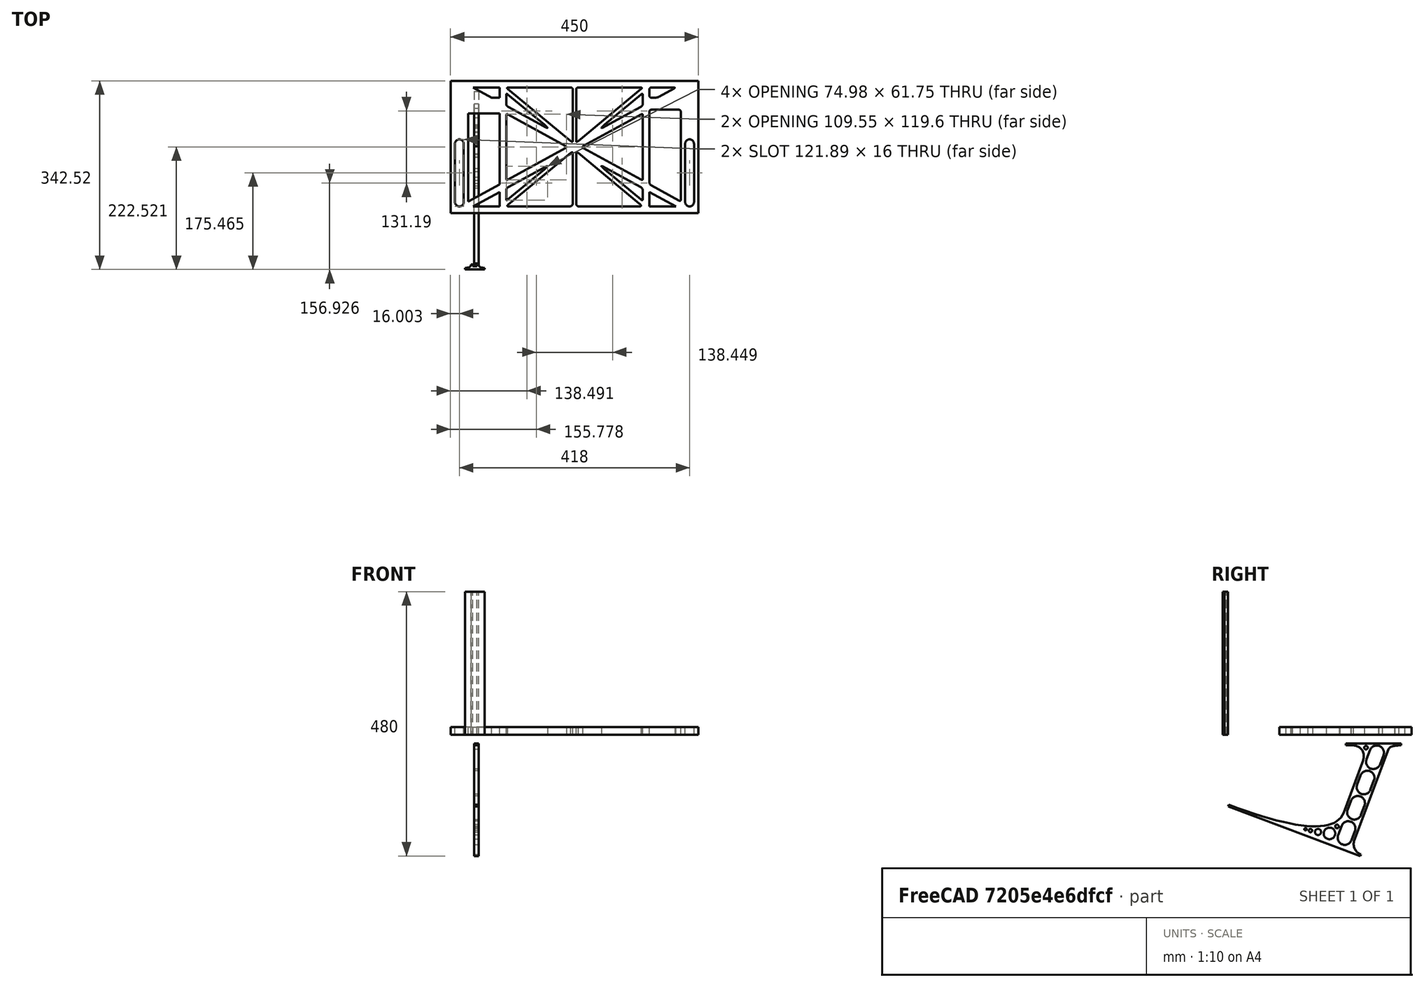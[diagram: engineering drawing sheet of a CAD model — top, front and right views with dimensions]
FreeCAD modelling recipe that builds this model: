
FCSTD DOCUMENT  (FreeCAD 0.19R0.19.2)
Label: laptopStand107
License: All rights reserved
LicenseURL: http://en.wikipedia.org/wiki/All_rights_reserved
objects: Sketcher::SketchObject×3, Part::Extrusion×3
note: 6 computed .brp shape members not serialized (recipe doc carries the construction recipe); baked Part::Feature solids carry a one-line shape summary decoded from their .brp

FEATURE [Sketcher::SketchObject] Sketch
  FullyConstrained = true
  sketch-geometry (292):
    g0: LineSegment StartX=-10.9272 StartY=-82.7794 StartZ=0 EndX=46.0728 EndY=-51.4823 EndZ=0
    g1: LineSegment StartX=366.073 StartY=-91.7794 StartZ=0 EndX=318.073 EndY=-65.424 EndZ=0
    g2: LineSegment StartX=-10.9272 StartY=77.3346 StartZ=0 EndX=-10.9272 EndY=-82.7794 EndZ=0
    g3: LineSegment StartX=-1.92719 StartY=-91.7794 StartZ=0 EndX=46.0728 EndY=-91.7794 EndZ=0
    g4: LineSegment StartX=318.073 StartY=-65.424 StartZ=0 EndX=318.073 EndY=-91.7794 EndZ=0
    g5: LineSegment StartX=318.073 StartY=-91.7794 StartZ=0 EndX=366.073 EndY=-91.7794 EndZ=0
    g6: LineSegment StartX=46.0728 StartY=-65.424 StartZ=0 EndX=-1.92719 EndY=-91.7794 EndZ=0
    g7: LineSegment StartX=46.0728 StartY=-65.424 StartZ=0 EndX=46.0728 EndY=-91.7794 EndZ=0
    g8: LineSegment StartX=46.0728 StartY=77.3346 StartZ=0 EndX=46.0728 EndY=-51.4823 EndZ=0
    g9: LineSegment StartX=-42.9272 StartY=136.221 StartZ=0 EndX=-42.9272 EndY=-103.779 EndZ=0
    g10: LineSegment StartX=407.073 StartY=136.221 StartZ=0 EndX=407.073 EndY=-103.779 EndZ=0
    g11: ArcOfCircle CenterX=-26.9272 CenterY=22.1087 CenterZ=0 NormalX=0 NormalY=0 NormalZ=1 AngleXU=0 Radius=8 StartAngle=1e-16 EndAngle=3.14159
    g12: ArcOfCircle CenterX=-26.9272 CenterY=-83.7794 CenterZ=0 NormalX=0 NormalY=0 NormalZ=1 AngleXU=0 Radius=8 StartAngle=3.14159 EndAngle=6.28319
    g13: LineSegment StartX=-34.9272 StartY=22.1087 StartZ=0 EndX=-34.9272 EndY=-83.7794 EndZ=0
    g14: LineSegment StartX=-18.9272 StartY=22.1087 StartZ=0 EndX=-18.9272 EndY=-83.7794 EndZ=0
    g15: ArcOfCircle CenterX=391.073 CenterY=22.1087 CenterZ=0 NormalX=0 NormalY=0 NormalZ=1 AngleXU=0 Radius=8 StartAngle=-4.4e-15 EndAngle=3.14159
    g16: LineSegment StartX=399.073 StartY=22.1087 StartZ=0 EndX=399.073 EndY=-83.7794 EndZ=0
    g17: LineSegment StartX=383.073 StartY=22.1087 StartZ=0 EndX=383.073 EndY=-83.7794 EndZ=0
    g18: ArcOfCircle CenterX=391.073 CenterY=-83.7794 CenterZ=0 NormalX=0 NormalY=0 NormalZ=1 AngleXU=0 Radius=8 StartAngle=3.14159 EndAngle=6.28319
    g19: Circle CenterX=175.022 CenterY=27.0628 CenterZ=0 NormalX=0 NormalY=0 NormalZ=1 AngleXU=0 Radius=1
    g20: Circle CenterX=179.022 CenterY=24.8665 CenterZ=0 NormalX=0 NormalY=0 NormalZ=1 AngleXU=0 Radius=1
    g21: Circle CenterX=179.022 CenterY=27.0628 CenterZ=0 NormalX=0 NormalY=0 NormalZ=1 AngleXU=0 Radius=1
    g22: BSplineCurve PolesCount=3 KnotsCount=2 Degree=2 IsPeriodic=0
    g23: GeomPoint X=175.022 Y=27.0628 Z=0
    g24: GeomPoint X=179.022 Y=27.0628 Z=0
    g25: Circle CenterX=189.124 CenterY=27.0628 CenterZ=0 NormalX=0 NormalY=0 NormalZ=1 AngleXU=0 Radius=1
    g26: Circle CenterX=185.124 CenterY=24.8665 CenterZ=0 NormalX=0 NormalY=0 NormalZ=1 AngleXU=0 Radius=1
    g27: Circle CenterX=185.124 CenterY=27.0628 CenterZ=0 NormalX=0 NormalY=0 NormalZ=1 AngleXU=0 Radius=1
    g28: BSplineCurve PolesCount=3 KnotsCount=2 Degree=2 IsPeriodic=0
    g29: GeomPoint X=189.124 Y=27.0628 Z=0
    g30: GeomPoint X=185.124 Y=27.0628 Z=0
    g31: Circle CenterX=175.022 CenterY=5.37834 CenterZ=0 NormalX=0 NormalY=0 NormalZ=1 AngleXU=0 Radius=1
    g32: Circle CenterX=179.022 CenterY=7.57463 CenterZ=0 NormalX=0 NormalY=0 NormalZ=1 AngleXU=0 Radius=1
    g33: Circle CenterX=179.022 CenterY=5.34704 CenterZ=0 NormalX=0 NormalY=0 NormalZ=1 AngleXU=0 Radius=1
    g34: BSplineCurve PolesCount=3 KnotsCount=2 Degree=2 IsPeriodic=0
    g35: GeomPoint X=175.022 Y=5.37834 Z=0
    g36: GeomPoint X=179.022 Y=5.34704 Z=0
    g37: Circle CenterX=189.124 CenterY=5.37834 CenterZ=0 NormalX=0 NormalY=0 NormalZ=1 AngleXU=0 Radius=1
    g38: Circle CenterX=185.124 CenterY=7.57463 CenterZ=0 NormalX=0 NormalY=0 NormalZ=1 AngleXU=0 Radius=1
    g39: Circle CenterX=185.124 CenterY=5.34704 CenterZ=0 NormalX=0 NormalY=0 NormalZ=1 AngleXU=0 Radius=1
    g40: BSplineCurve PolesCount=3 KnotsCount=2 Degree=2 IsPeriodic=0
    g41: GeomPoint X=189.124 Y=5.37834 Z=0
    g42: GeomPoint X=185.124 Y=5.34704 Z=0
    g43: Circle CenterX=165.871 CenterY=18.1458 CenterZ=0 NormalX=0 NormalY=0 NormalZ=1 AngleXU=0 Radius=1
    g44: Circle CenterX=169.377 CenterY=16.2206 CenterZ=0 NormalX=0 NormalY=0 NormalZ=1 AngleXU=0 Radius=1
    g45: Circle CenterX=165.871 CenterY=14.2954 CenterZ=0 NormalX=0 NormalY=0 NormalZ=1 AngleXU=0 Radius=1
    g46: BSplineCurve PolesCount=3 KnotsCount=2 Degree=2 IsPeriodic=0
    g47: GeomPoint X=165.871 Y=18.1458 Z=0
    g48: GeomPoint X=165.871 Y=14.2954 Z=0
    g49: Circle CenterX=198.275 CenterY=18.1458 CenterZ=0 NormalX=0 NormalY=0 NormalZ=1 AngleXU=0 Radius=1
    g50: Circle CenterX=194.768 CenterY=16.2206 CenterZ=0 NormalX=0 NormalY=0 NormalZ=1 AngleXU=0 Radius=1
    g51: Circle CenterX=198.275 CenterY=14.2954 CenterZ=0 NormalX=0 NormalY=0 NormalZ=1 AngleXU=0 Radius=1
    g52: BSplineCurve PolesCount=3 KnotsCount=2 Degree=2 IsPeriodic=0
    g53: GeomPoint X=198.275 Y=18.1458 Z=0
    g54: GeomPoint X=198.275 Y=14.2954 Z=0
    g55: LineSegment StartX=407.073 StartY=-103.779 StartZ=0 EndX=-42.9272 EndY=-103.779 EndZ=0
    g56: LineSegment StartX=407.073 StartY=136.221 StartZ=0 EndX=-42.9272 EndY=136.221 EndZ=0
    g57: LineSegment StartX=46.0728 StartY=77.3346 StartZ=0 EndX=-10.9272 EndY=77.3346 EndZ=0
    g58: LineSegment StartX=46.0728 StartY=105.865 StartZ=0 EndX=31.5028 EndY=105.865 EndZ=0
    g59: LineSegment StartX=46.0728 StartY=124.221 StartZ=0 EndX=46.0728 EndY=105.865 EndZ=0
    g60: LineSegment StartX=-1.92719 StartY=124.221 StartZ=0 EndX=31.5028 EndY=105.865 EndZ=0
    g61: LineSegment StartX=46.0728 StartY=124.221 StartZ=0 EndX=-1.92719 EndY=124.221 EndZ=0
    g62: Circle CenterX=125.607 CenterY=54.1951 CenterZ=0 NormalX=0 NormalY=0 NormalZ=1 AngleXU=0 Radius=1
    g63: Circle CenterX=139.632 CenterY=46.4944 CenterZ=0 NormalX=0 NormalY=0 NormalZ=1 AngleXU=0 Radius=1
    g64: Circle CenterX=127.326 CenterY=56.7187 CenterZ=0 NormalX=0 NormalY=0 NormalZ=1 AngleXU=0 Radius=1
    g65: BSplineCurve PolesCount=3 KnotsCount=2 Degree=2 IsPeriodic=0
    g66: GeomPoint X=125.607 Y=54.1951 Z=0
    g67: GeomPoint X=127.326 Y=56.7187 Z=0
    g68: Circle CenterX=236.821 CenterY=56.7187 CenterZ=0 NormalX=0 NormalY=0 NormalZ=1 AngleXU=0 Radius=1
    g69: Circle CenterX=224.513 CenterY=46.4944 CenterZ=0 NormalX=0 NormalY=0 NormalZ=1 AngleXU=0 Radius=1
    g70: Circle CenterX=238.538 CenterY=54.1951 CenterZ=0 NormalX=0 NormalY=0 NormalZ=1 AngleXU=0 Radius=1
    g71: BSplineCurve PolesCount=3 KnotsCount=2 Degree=2 IsPeriodic=0
    g72: GeomPoint X=236.821 Y=56.7187 Z=0
    g73: GeomPoint X=238.538 Y=54.1951 Z=0
    g74: Circle CenterX=238.538 CenterY=-21.7539 CenterZ=0 NormalX=0 NormalY=0 NormalZ=1 AngleXU=0 Radius=1
    g75: Circle CenterX=224.513 CenterY=-14.0532 CenterZ=0 NormalX=0 NormalY=0 NormalZ=1 AngleXU=0 Radius=1
    g76: Circle CenterX=236.821 CenterY=-24.2775 CenterZ=0 NormalX=0 NormalY=0 NormalZ=1 AngleXU=0 Radius=1
    g77: BSplineCurve PolesCount=3 KnotsCount=2 Degree=2 IsPeriodic=0
    g78: GeomPoint X=238.538 Y=-21.7539 Z=0
    g79: GeomPoint X=236.821 Y=-24.2775 Z=0
    g80: Circle CenterX=125.607 CenterY=-21.7539 CenterZ=0 NormalX=0 NormalY=0 NormalZ=1 AngleXU=0 Radius=1
    g81: Circle CenterX=139.632 CenterY=-14.0532 CenterZ=0 NormalX=0 NormalY=0 NormalZ=1 AngleXU=0 Radius=1
    g82: Circle CenterX=127.325 CenterY=-24.2775 CenterZ=0 NormalX=0 NormalY=0 NormalZ=1 AngleXU=0 Radius=1
    g83: BSplineCurve PolesCount=3 KnotsCount=2 Degree=2 IsPeriodic=0
    g84: GeomPoint X=125.607 Y=-21.7539 Z=0
    g85: GeomPoint X=127.325 Y=-24.2775 Z=0
    g86: Circle CenterX=302.996 CenterY=111.695 CenterZ=0 NormalX=0 NormalY=0 NormalZ=1 AngleXU=0 Radius=1
    g87: Circle CenterX=306.073 CenterY=114.251 CenterZ=0 NormalX=0 NormalY=0 NormalZ=1 AngleXU=0 Radius=1
    g88: Circle CenterX=306.073 CenterY=110.251 CenterZ=0 NormalX=0 NormalY=0 NormalZ=1 AngleXU=0 Radius=1
    g89: BSplineCurve PolesCount=3 KnotsCount=2 Degree=2 IsPeriodic=0
    g90: GeomPoint X=302.996 Y=111.695 Z=0
    g91: GeomPoint X=306.073 Y=110.251 Z=0
    g92: Circle CenterX=306.073 CenterY=95.2763 CenterZ=0 NormalX=0 NormalY=0 NormalZ=1 AngleXU=0 Radius=1
    g93: Circle CenterX=306.073 CenterY=91.2763 CenterZ=0 NormalX=0 NormalY=0 NormalZ=1 AngleXU=0 Radius=1
    g94: Circle CenterX=302.567 CenterY=89.3511 CenterZ=0 NormalX=0 NormalY=0 NormalZ=1 AngleXU=0 Radius=1
    g95: BSplineCurve PolesCount=3 KnotsCount=2 Degree=2 IsPeriodic=0
    g96: GeomPoint X=306.073 Y=95.2763 Z=0
    g97: GeomPoint X=302.567 Y=89.3511 Z=0
    g98: LineSegment StartX=306.073 StartY=110.251 StartZ=0 EndX=306.073 EndY=95.2763 EndZ=0
    g99: LineSegment StartX=302.996 StartY=111.695 StartZ=0 EndX=236.821 EndY=56.7187 EndZ=0
    g100: LineSegment StartX=238.538 StartY=54.1951 StartZ=0 EndX=302.567 EndY=89.3511 EndZ=0
    g101: Circle CenterX=61.1496 CenterY=111.695 CenterZ=0 NormalX=0 NormalY=0 NormalZ=1 AngleXU=0 Radius=1
    g102: Circle CenterX=58.0728 CenterY=114.251 CenterZ=0 NormalX=0 NormalY=0 NormalZ=1 AngleXU=0 Radius=1
    g103: Circle CenterX=58.0728 CenterY=110.251 CenterZ=0 NormalX=0 NormalY=0 NormalZ=1 AngleXU=0 Radius=1
    g104: BSplineCurve PolesCount=3 KnotsCount=2 Degree=2 IsPeriodic=0
    g105: GeomPoint X=61.1496 Y=111.695 Z=0
    g106: GeomPoint X=58.0728 Y=110.251 Z=0
    g107: Circle CenterX=61.5791 CenterY=89.3511 CenterZ=0 NormalX=0 NormalY=0 NormalZ=1 AngleXU=0 Radius=1
    g108: Circle CenterX=58.0728 CenterY=91.2763 CenterZ=0 NormalX=0 NormalY=0 NormalZ=1 AngleXU=0 Radius=1
    g109: Circle CenterX=58.0728 CenterY=95.2763 CenterZ=0 NormalX=0 NormalY=0 NormalZ=1 AngleXU=0 Radius=1
    g110: BSplineCurve PolesCount=3 KnotsCount=2 Degree=2 IsPeriodic=0
    g111: GeomPoint X=61.5791 Y=89.3511 Z=0
    g112: GeomPoint X=58.0728 Y=95.2763 Z=0
    g113: LineSegment StartX=58.0728 StartY=110.251 StartZ=0 EndX=58.0728 EndY=95.2763 EndZ=0
    g114: LineSegment StartX=61.1496 StartY=111.695 StartZ=0 EndX=127.326 EndY=56.7187 EndZ=0
    g115: LineSegment StartX=125.607 StartY=54.1951 StartZ=0 EndX=61.5791 EndY=89.3511 EndZ=0
    g116: Circle CenterX=61.5791 CenterY=-56.9099 CenterZ=0 NormalX=0 NormalY=0 NormalZ=1 AngleXU=0 Radius=1
    g117: Circle CenterX=58.0728 CenterY=-58.8351 CenterZ=0 NormalX=0 NormalY=0 NormalZ=1 AngleXU=0 Radius=1
    g118: Circle CenterX=58.0728 CenterY=-62.8351 CenterZ=0 NormalX=0 NormalY=0 NormalZ=1 AngleXU=0 Radius=1
    g119: BSplineCurve PolesCount=3 KnotsCount=2 Degree=2 IsPeriodic=0
    g120: GeomPoint X=61.5791 Y=-56.9099 Z=0
    g121: GeomPoint X=58.0728 Y=-62.8351 Z=0
    g122: Circle CenterX=58.0728 CenterY=-77.8102 CenterZ=0 NormalX=0 NormalY=0 NormalZ=1 AngleXU=0 Radius=1
    g123: Circle CenterX=58.0728 CenterY=-81.8102 CenterZ=0 NormalX=0 NormalY=0 NormalZ=1 AngleXU=0 Radius=1
    g124: Circle CenterX=61.1496 CenterY=-79.2541 CenterZ=0 NormalX=0 NormalY=0 NormalZ=1 AngleXU=0 Radius=1
    g125: BSplineCurve PolesCount=3 KnotsCount=2 Degree=2 IsPeriodic=0
    g126: GeomPoint X=58.0728 Y=-77.8102 Z=0
    g127: GeomPoint X=61.1496 Y=-79.2541 Z=0
    g128: LineSegment StartX=58.0728 StartY=-62.8351 StartZ=0 EndX=58.0728 EndY=-77.8102 EndZ=0
    g129: LineSegment StartX=61.1496 StartY=-79.2541 StartZ=0 EndX=127.325 EndY=-24.2775 EndZ=0
    g130: LineSegment StartX=125.607 StartY=-21.7539 StartZ=0 EndX=61.5791 EndY=-56.9099 EndZ=0
    g131: Circle CenterX=302.567 CenterY=-56.9099 CenterZ=0 NormalX=0 NormalY=0 NormalZ=1 AngleXU=0 Radius=1
    g132: Circle CenterX=306.073 CenterY=-58.8351 CenterZ=0 NormalX=0 NormalY=0 NormalZ=1 AngleXU=0 Radius=1
    g133: Circle CenterX=306.073 CenterY=-62.8351 CenterZ=0 NormalX=0 NormalY=0 NormalZ=1 AngleXU=0 Radius=1
    g134: BSplineCurve PolesCount=3 KnotsCount=2 Degree=2 IsPeriodic=0
    g135: GeomPoint X=302.567 Y=-56.9099 Z=0
    g136: GeomPoint X=306.073 Y=-62.8351 Z=0
    g137: Circle CenterX=302.996 CenterY=-79.2541 CenterZ=0 NormalX=0 NormalY=0 NormalZ=1 AngleXU=0 Radius=1
    g138: Circle CenterX=306.073 CenterY=-81.8102 CenterZ=0 NormalX=0 NormalY=0 NormalZ=1 AngleXU=0 Radius=1
    g139: Circle CenterX=306.073 CenterY=-77.8102 CenterZ=0 NormalX=0 NormalY=0 NormalZ=1 AngleXU=0 Radius=1
    g140: BSplineCurve PolesCount=3 KnotsCount=2 Degree=2 IsPeriodic=0
    g141: GeomPoint X=302.996 Y=-79.2541 Z=0
    g142: GeomPoint X=306.073 Y=-77.8102 Z=0
    g143: LineSegment StartX=306.073 StartY=-62.8351 StartZ=0 EndX=306.073 EndY=-77.8102 EndZ=0
    g144: LineSegment StartX=302.996 StartY=-79.2541 StartZ=0 EndX=236.821 EndY=-24.2775 EndZ=0
    g145: LineSegment StartX=238.538 StartY=-21.7539 StartZ=0 EndX=302.567 EndY=-56.9099 EndZ=0
    g146: Circle CenterX=61.6457 CenterY=-88.8112 CenterZ=0 NormalX=0 NormalY=0 NormalZ=1 AngleXU=0 Radius=1
    g147: Circle CenterX=58.0728 CenterY=-91.7794 CenterZ=0 NormalX=0 NormalY=0 NormalZ=1 AngleXU=0 Radius=1
    g148: Circle CenterX=63.9135 CenterY=-91.7794 CenterZ=0 NormalX=0 NormalY=0 NormalZ=1 AngleXU=0 Radius=1
    g149: BSplineCurve PolesCount=3 KnotsCount=2 Degree=2 IsPeriodic=0
    g150: GeomPoint X=61.6457 Y=-88.8112 Z=0
    g151: GeomPoint X=63.9135 Y=-91.7794 Z=0
    g152: Circle CenterX=179.022 CenterY=-85.8163 CenterZ=0 NormalX=0 NormalY=0 NormalZ=1 AngleXU=0 Radius=1
    g153: Circle CenterX=179.022 CenterY=-91.7794 CenterZ=0 NormalX=0 NormalY=0 NormalZ=1 AngleXU=0 Radius=1
    g154: Circle CenterX=171.895 CenterY=-91.7794 CenterZ=0 NormalX=0 NormalY=0 NormalZ=1 AngleXU=0 Radius=1
    g155: BSplineCurve PolesCount=3 KnotsCount=2 Degree=2 IsPeriodic=0
    g156: GeomPoint X=179.022 Y=-85.8163 Z=0
    g157: GeomPoint X=171.895 Y=-91.7794 Z=0
    g158: Circle CenterX=185.124 CenterY=-86.2028 CenterZ=0 NormalX=0 NormalY=0 NormalZ=1 AngleXU=0 Radius=1
    g159: Circle CenterX=185.124 CenterY=-91.7794 CenterZ=0 NormalX=0 NormalY=0 NormalZ=1 AngleXU=0 Radius=1
    g160: Circle CenterX=191.747 CenterY=-91.7794 CenterZ=0 NormalX=0 NormalY=0 NormalZ=1 AngleXU=0 Radius=1
    g161: BSplineCurve PolesCount=3 KnotsCount=2 Degree=2 IsPeriodic=0
    g162: GeomPoint X=185.124 Y=-86.2028 Z=0
    g163: GeomPoint X=191.747 Y=-91.7794 Z=0
    g164: Circle CenterX=299.888 CenterY=-86.6413 CenterZ=0 NormalX=0 NormalY=0 NormalZ=1 AngleXU=0 Radius=1
    g165: Circle CenterX=306.073 CenterY=-91.7794 CenterZ=0 NormalX=0 NormalY=0 NormalZ=1 AngleXU=0 Radius=1
    g166: Circle CenterX=298.776 CenterY=-91.7794 CenterZ=0 NormalX=0 NormalY=0 NormalZ=1 AngleXU=0 Radius=1
    g167: BSplineCurve PolesCount=3 KnotsCount=2 Degree=2 IsPeriodic=0
    g168: GeomPoint X=299.888 Y=-86.6413 Z=0
    g169: GeomPoint X=298.776 Y=-91.7794 Z=0
    g170: LineSegment StartX=189.124 StartY=5.37834 StartZ=0 EndX=299.888 EndY=-86.6413 EndZ=0
    g171: LineSegment StartX=298.776 StartY=-91.7794 StartZ=0 EndX=191.747 EndY=-91.7794 EndZ=0
    g172: LineSegment StartX=185.124 StartY=-86.2028 StartZ=0 EndX=185.124 EndY=5.34704 EndZ=0
    g173: LineSegment StartX=179.022 StartY=5.34704 StartZ=0 EndX=179.022 EndY=-85.8163 EndZ=0
    g174: LineSegment StartX=171.895 StartY=-91.7794 StartZ=0 EndX=63.9135 EndY=-91.7794 EndZ=0
    g175: LineSegment StartX=61.6457 StartY=-88.8112 StartZ=0 EndX=175.022 EndY=5.37834 EndZ=0
    g176: Circle CenterX=302.073 CenterY=124.221 CenterZ=0 NormalX=0 NormalY=0 NormalZ=1 AngleXU=0 Radius=1
    g177: Circle CenterX=306.073 CenterY=124.221 CenterZ=0 NormalX=0 NormalY=0 NormalZ=1 AngleXU=0 Radius=1
    g178: Circle CenterX=302.996 CenterY=121.665 CenterZ=0 NormalX=0 NormalY=0 NormalZ=1 AngleXU=0 Radius=1
    g179: BSplineCurve PolesCount=3 KnotsCount=2 Degree=2 IsPeriodic=0
    g180: GeomPoint X=302.073 Y=124.221 Z=0
    g181: GeomPoint X=302.996 Y=121.665 Z=0
    g182: Circle CenterX=189.124 CenterY=124.221 CenterZ=0 NormalX=0 NormalY=0 NormalZ=1 AngleXU=0 Radius=1
    g183: Circle CenterX=185.124 CenterY=124.221 CenterZ=0 NormalX=0 NormalY=0 NormalZ=1 AngleXU=0 Radius=1
    g184: Circle CenterX=185.124 CenterY=120.221 CenterZ=0 NormalX=0 NormalY=0 NormalZ=1 AngleXU=0 Radius=1
    g185: BSplineCurve PolesCount=3 KnotsCount=2 Degree=2 IsPeriodic=0
    g186: GeomPoint X=189.124 Y=124.221 Z=0
    g187: GeomPoint X=185.124 Y=120.221 Z=0
    g188: Circle CenterX=175.022 CenterY=124.221 CenterZ=0 NormalX=0 NormalY=0 NormalZ=1 AngleXU=0 Radius=1
    g189: Circle CenterX=179.022 CenterY=124.221 CenterZ=0 NormalX=0 NormalY=0 NormalZ=1 AngleXU=0 Radius=1
    g190: Circle CenterX=179.022 CenterY=120.221 CenterZ=0 NormalX=0 NormalY=0 NormalZ=1 AngleXU=0 Radius=1
    g191: BSplineCurve PolesCount=3 KnotsCount=2 Degree=2 IsPeriodic=0
    g192: GeomPoint X=175.022 Y=124.221 Z=0
    g193: GeomPoint X=179.022 Y=120.221 Z=0
    g194: Circle CenterX=62.0728 CenterY=124.221 CenterZ=0 NormalX=0 NormalY=0 NormalZ=1 AngleXU=0 Radius=1
    g195: Circle CenterX=58.0728 CenterY=124.221 CenterZ=0 NormalX=0 NormalY=0 NormalZ=1 AngleXU=0 Radius=1
    g196: Circle CenterX=61.1496 CenterY=121.665 CenterZ=0 NormalX=0 NormalY=0 NormalZ=1 AngleXU=0 Radius=1
    g197: BSplineCurve PolesCount=3 KnotsCount=2 Degree=2 IsPeriodic=0
    g198: GeomPoint X=62.0728 Y=124.221 Z=0
    g199: GeomPoint X=61.1496 Y=121.665 Z=0
    g200: LineSegment StartX=62.0728 StartY=124.221 StartZ=0 EndX=175.022 EndY=124.221 EndZ=0
    g201: LineSegment StartX=179.022 StartY=120.221 StartZ=0 EndX=179.022 EndY=27.0628 EndZ=0
    g202: LineSegment StartX=185.124 StartY=27.0628 StartZ=0 EndX=185.124 EndY=120.221 EndZ=0
    g203: LineSegment StartX=189.124 StartY=124.221 StartZ=0 EndX=302.073 EndY=124.221 EndZ=0
    g204: LineSegment StartX=302.996 StartY=121.665 StartZ=0 EndX=189.124 EndY=27.0628 EndZ=0
    g205: LineSegment StartX=175.022 StartY=27.0628 StartZ=0 EndX=61.1496 EndY=121.665 EndZ=0
    g206: Circle CenterX=61.5791 CenterY=75.4095 CenterZ=0 NormalX=0 NormalY=0 NormalZ=1 AngleXU=0 Radius=1
    g207: Circle CenterX=58.0728 CenterY=77.3346 CenterZ=0 NormalX=0 NormalY=0 NormalZ=1 AngleXU=0 Radius=1
    g208: Circle CenterX=58.0728 CenterY=73.3346 CenterZ=0 NormalX=0 NormalY=0 NormalZ=1 AngleXU=0 Radius=1
    g209: BSplineCurve PolesCount=3 KnotsCount=2 Degree=2 IsPeriodic=0
    g210: GeomPoint X=61.5791 Y=75.4095 Z=0
    g211: GeomPoint X=58.0728 Y=73.3346 Z=0
    g212: Circle CenterX=58.0728 CenterY=-40.8935 CenterZ=0 NormalX=0 NormalY=0 NormalZ=1 AngleXU=0 Radius=1
    g213: Circle CenterX=58.0728 CenterY=-44.8935 CenterZ=0 NormalX=0 NormalY=0 NormalZ=1 AngleXU=0 Radius=1
    g214: Circle CenterX=61.5791 CenterY=-42.9683 CenterZ=0 NormalX=0 NormalY=0 NormalZ=1 AngleXU=0 Radius=1
    g215: BSplineCurve PolesCount=3 KnotsCount=2 Degree=2 IsPeriodic=0
    g216: GeomPoint X=58.0728 Y=-40.8935 Z=0
    g217: GeomPoint X=61.5791 Y=-42.9683 Z=0
    g218: LineSegment StartX=61.5791 StartY=-42.9683 StartZ=0 EndX=165.871 EndY=14.2954 EndZ=0
    g219: LineSegment StartX=165.871 StartY=18.1458 StartZ=0 EndX=61.5791 EndY=75.4095 EndZ=0
    g220: LineSegment StartX=58.0728 StartY=73.3346 StartZ=0 EndX=58.0728 EndY=-40.8935 EndZ=0
    g221: Circle CenterX=302.567 CenterY=-42.9683 CenterZ=0 NormalX=0 NormalY=0 NormalZ=1 AngleXU=0 Radius=1
    g222: Circle CenterX=306.073 CenterY=-44.8935 CenterZ=0 NormalX=0 NormalY=0 NormalZ=1 AngleXU=0 Radius=1
    g223: Circle CenterX=306.073 CenterY=-40.8935 CenterZ=0 NormalX=0 NormalY=0 NormalZ=1 AngleXU=0 Radius=1
    g224: BSplineCurve PolesCount=3 KnotsCount=2 Degree=2 IsPeriodic=0
    g225: GeomPoint X=302.567 Y=-42.9683 Z=0
    g226: GeomPoint X=306.073 Y=-40.8935 Z=0
    g227: Circle CenterX=306.073 CenterY=73.3346 CenterZ=0 NormalX=0 NormalY=0 NormalZ=1 AngleXU=0 Radius=1
    g228: Circle CenterX=306.073 CenterY=77.3346 CenterZ=0 NormalX=0 NormalY=0 NormalZ=1 AngleXU=0 Radius=1
    g229: Circle CenterX=302.567 CenterY=75.4095 CenterZ=0 NormalX=0 NormalY=0 NormalZ=1 AngleXU=0 Radius=1
    g230: BSplineCurve PolesCount=3 KnotsCount=2 Degree=2 IsPeriodic=0
    g231: GeomPoint X=306.073 Y=73.3346 Z=0
    g232: GeomPoint X=302.567 Y=75.4095 Z=0
    g233: LineSegment StartX=302.567 StartY=-42.9683 StartZ=0 EndX=198.275 EndY=14.2954 EndZ=0
    g234: LineSegment StartX=198.275 StartY=18.1458 StartZ=0 EndX=302.567 EndY=75.4095 EndZ=0
    g235: LineSegment StartX=306.073 StartY=73.3346 StartZ=0 EndX=306.073 EndY=-40.8935 EndZ=0
    g236: LineSegment StartX=322.073 StartY=105.865 StartZ=0 EndX=328.643 EndY=105.865 EndZ=0
    g237: LineSegment StartX=318.073 StartY=120.221 StartZ=0 EndX=318.073 EndY=109.865 EndZ=0
    g238: LineSegment StartX=336.157 StartY=107.779 StartZ=0 EndX=362.567 EndY=122.294 EndZ=0
    g239: Circle CenterX=362.073 CenterY=124.221 CenterZ=0 NormalX=0 NormalY=0 NormalZ=1 AngleXU=0 Radius=1
    g240: Circle CenterX=366.073 CenterY=124.221 CenterZ=0 NormalX=0 NormalY=0 NormalZ=1 AngleXU=0 Radius=1
    g241: Circle CenterX=362.567 CenterY=122.294 CenterZ=0 NormalX=0 NormalY=0 NormalZ=1 AngleXU=0 Radius=1
    g242: BSplineCurve PolesCount=3 KnotsCount=2 Degree=2 IsPeriodic=0
    g243: GeomPoint X=362.073 Y=124.221 Z=0
    g244: GeomPoint X=362.567 Y=122.294 Z=0
    g245: Circle CenterX=322.073 CenterY=124.221 CenterZ=0 NormalX=0 NormalY=0 NormalZ=1 AngleXU=0 Radius=1
    g246: Circle CenterX=318.073 CenterY=124.221 CenterZ=0 NormalX=0 NormalY=0 NormalZ=1 AngleXU=0 Radius=1
    g247: Circle CenterX=318.073 CenterY=120.221 CenterZ=0 NormalX=0 NormalY=0 NormalZ=1 AngleXU=0 Radius=1
    g248: BSplineCurve PolesCount=3 KnotsCount=2 Degree=2 IsPeriodic=0
    g249: GeomPoint X=322.073 Y=124.221 Z=0
    g250: GeomPoint X=318.073 Y=120.221 Z=0
    g251: Circle CenterX=322.073 CenterY=105.865 CenterZ=0 NormalX=0 NormalY=0 NormalZ=1 AngleXU=0 Radius=1
    g252: Circle CenterX=318.073 CenterY=105.865 CenterZ=0 NormalX=0 NormalY=0 NormalZ=1 AngleXU=0 Radius=1
    g253: Circle CenterX=318.073 CenterY=109.865 CenterZ=0 NormalX=0 NormalY=0 NormalZ=1 AngleXU=0 Radius=1
    g254: BSplineCurve PolesCount=3 KnotsCount=2 Degree=2 IsPeriodic=0
    g255: GeomPoint X=322.073 Y=105.865 Z=0
    g256: GeomPoint X=318.073 Y=109.865 Z=0
    g257: Circle CenterX=336.157 CenterY=107.779 CenterZ=0 NormalX=0 NormalY=0 NormalZ=1 AngleXU=0 Radius=1
    g258: Circle CenterX=332.651 CenterY=105.853 CenterZ=0 NormalX=0 NormalY=0 NormalZ=1 AngleXU=0 Radius=1
    g259: Circle CenterX=328.643 CenterY=105.865 CenterZ=0 NormalX=0 NormalY=0 NormalZ=1 AngleXU=0 Radius=1
    g260: BSplineCurve PolesCount=3 KnotsCount=2 Degree=2 IsPeriodic=0
    g261: GeomPoint X=336.157 Y=107.779 Z=0
    g262: GeomPoint X=328.643 Y=105.865 Z=0
    g263: LineSegment StartX=322.073 StartY=124.221 StartZ=0 EndX=362.073 EndY=124.221 EndZ=0
    g264: Circle CenterX=371.567 CenterY=-80.8644 CenterZ=0 NormalX=0 NormalY=0 NormalZ=1 AngleXU=0 Radius=1
    g265: Circle CenterX=375.073 CenterY=-82.7896 CenterZ=0 NormalX=0 NormalY=0 NormalZ=1 AngleXU=0 Radius=1
    g266: Circle CenterX=375.073 CenterY=-78.7896 CenterZ=0 NormalX=0 NormalY=0 NormalZ=1 AngleXU=0 Radius=1
    g267: BSplineCurve PolesCount=3 KnotsCount=2 Degree=2 IsPeriodic=0
    g268: GeomPoint X=371.567 Y=-80.8644 Z=0
    g269: GeomPoint X=375.073 Y=-78.7896 Z=0
    g270: Circle CenterX=321.579 CenterY=-53.4075 CenterZ=0 NormalX=0 NormalY=0 NormalZ=1 AngleXU=0 Radius=1
    g271: Circle CenterX=318.073 CenterY=-51.4823 CenterZ=0 NormalX=0 NormalY=0 NormalZ=1 AngleXU=0 Radius=1
    g272: Circle CenterX=318.073 CenterY=-47.4823 CenterZ=0 NormalX=0 NormalY=0 NormalZ=1 AngleXU=0 Radius=1
    g273: BSplineCurve PolesCount=3 KnotsCount=2 Degree=2 IsPeriodic=0
    g274: GeomPoint X=321.579 Y=-53.4075 Z=0
    g275: GeomPoint X=318.073 Y=-47.4823 Z=0
    g276: Circle CenterX=318.073 CenterY=79.9235 CenterZ=0 NormalX=0 NormalY=0 NormalZ=1 AngleXU=0 Radius=1
    g277: Circle CenterX=318.073 CenterY=83.9235 CenterZ=0 NormalX=0 NormalY=0 NormalZ=1 AngleXU=0 Radius=1
    g278: Circle CenterX=322.073 CenterY=83.9235 CenterZ=0 NormalX=0 NormalY=0 NormalZ=1 AngleXU=0 Radius=1
    g279: BSplineCurve PolesCount=3 KnotsCount=2 Degree=2 IsPeriodic=0
    g280: GeomPoint X=318.073 Y=79.9235 Z=0
    g281: GeomPoint X=322.073 Y=83.9235 Z=0
    g282: Circle CenterX=375.073 CenterY=79.9235 CenterZ=0 NormalX=0 NormalY=0 NormalZ=1 AngleXU=0 Radius=1
    g283: Circle CenterX=375.073 CenterY=83.9235 CenterZ=0 NormalX=0 NormalY=0 NormalZ=1 AngleXU=0 Radius=1
    g284: Circle CenterX=371.073 CenterY=83.9235 CenterZ=0 NormalX=0 NormalY=0 NormalZ=1 AngleXU=0 Radius=1
    g285: BSplineCurve PolesCount=3 KnotsCount=2 Degree=2 IsPeriodic=0
    g286: GeomPoint X=375.073 Y=79.9235 Z=0
    g287: GeomPoint X=371.073 Y=83.9235 Z=0
    g288: LineSegment StartX=322.073 StartY=83.9235 StartZ=0 EndX=371.073 EndY=83.9235 EndZ=0
    g289: LineSegment StartX=375.073 StartY=79.9235 StartZ=0 EndX=375.073 EndY=-78.7896 EndZ=0
    g290: LineSegment StartX=371.567 StartY=-80.8644 StartZ=0 EndX=321.579 EndY=-53.4075 EndZ=0
    g291: LineSegment StartX=318.073 StartY=-47.4823 StartZ=0 EndX=318.073 EndY=79.9235 EndZ=0
  constraints (488):
    c: Horizontal(g3)
    c: Coincident(g4,g1)
    c: Coincident(g7,g6)
    c: Coincident(g0,g8)
    c: Block(g1)
    c: Block(g4)
    c: Block(g7)
    c: Block(g6)
    c: Block(g0)
    c: Block(g2)
    c: Block(g5)
    c: Block(g3)
    c: Vertical(g9)
    c: Vertical(g10)
    c: Block(g10)
    c: Block(g9)
    c: Tangent(g11,g14) = 1.5708
    c: Tangent(g11,g13) = -1.5708
    c: Tangent(g13,g12) = -1.5708
    c: Tangent(g14,g12) = 1.5708
    c: Vertical(g13)
    c: Equal(g11,g12)
    c: Block(g14)
    c: Block(g13)
    c: Tangent(g15,g16) = 1.5708
    c: Tangent(g16,g18) = 1.5708
    c: Equal(g15,g18)
    c: Coincident(g17,g15)
    c: Coincident(g17,g18)
    c: Block(g16)
    c: Block(g17)
    c: Weight(g19) = 1
    c: Equal(g19,g20)
    c: Equal(g19,g21)
    c: InternalAlignment(g19,g22)
    c: InternalAlignment(g20,g22)
    c: InternalAlignment(g21,g22)
    c: InternalAlignment(g23,g22)
    c: InternalAlignment(g24,g22)
    c: Weight(g25) = 1
    c: Equal(g25,g26)
    c: Equal(g25,g27)
    c: InternalAlignment(g25,g28)
    c: InternalAlignment(g26,g28)
    c: InternalAlignment(g27,g28)
    c: InternalAlignment(g29,g28)
    c: InternalAlignment(g30,g28)
    c: Block(g28)
    c: Block(g22)
    c: Weight(g31) = 1
    c: Equal(g31,g32)
    c: Equal(g31,g33)
    c: InternalAlignment(g31,g34)
    c: InternalAlignment(g32,g34)
    c: InternalAlignment(g33,g34)
    c: InternalAlignment(g35,g34)
    c: InternalAlignment(g36,g34)
    c: Weight(g37) = 1
    c: Equal(g37,g38)
    c: Equal(g37,g39)
    c: InternalAlignment(g37,g40)
    c: InternalAlignment(g38,g40)
    c: InternalAlignment(g39,g40)
    c: InternalAlignment(g41,g40)
    c: InternalAlignment(g42,g40)
    c: Block(g40)
    c: Block(g34)
    c: Weight(g43) = 1
    c: Equal(g43,g44)
    c: Equal(g43,g45)
    c: InternalAlignment(g43,g46)
    c: InternalAlignment(g44,g46)
    c: InternalAlignment(g45,g46)
    c: InternalAlignment(g47,g46)
    c: InternalAlignment(g48,g46)
    c: Weight(g49) = 1
    c: Equal(g49,g50)
    c: Equal(g49,g51)
    c: InternalAlignment(g49,g52)
    c: InternalAlignment(g50,g52)
    c: InternalAlignment(g51,g52)
    c: InternalAlignment(g53,g52)
    c: InternalAlignment(g54,g52)
    c: Block(g46)
    c: Block(g52)
    c: Coincident(g55,g10)
    c: Coincident(g55,g9)
    c: Horizontal(g55)
    c: Distance(g55) = 450
    c: Coincident(g56,g10)
    c: Coincident(g56,g9)
    c: Horizontal(g56)
    c: Horizontal(g57)
    c: Coincident(g8,g57)
    c: Horizontal(g58)
    c: Vertical(g59)
    c: Block(g59)
    c: Block(g58)
    c: Block(g57)
    c: Distance(g59) = 18.3554
    c: Coincident(g61,g59)
    c: Coincident(g61,g60)
    c: Horizontal(g61)
    c: Block(g61)
    c: Block(g60)
    c: Coincident(g58,g60)
    c: Coincident(g2,g57)
    c: Weight(g62) = 1
    c: Equal(g62,g63)
    c: Equal(g62,g64)
    c: InternalAlignment(g62,g65)
    c: InternalAlignment(g63,g65)
    c: InternalAlignment(g64,g65)
    c: InternalAlignment(g66,g65)
    c: InternalAlignment(g67,g65)
    c: Block(g65)
    c: Weight(g68) = 1
    c: Equal(g68,g69)
    c: Equal(g68,g70)
    c: InternalAlignment(g68,g71)
    c: InternalAlignment(g69,g71)
    c: InternalAlignment(g70,g71)
    c: InternalAlignment(g72,g71)
    c: InternalAlignment(g73,g71)
    c: Block(g71)
    c: Weight(g74) = 1
    c: Equal(g74,g75)
    c: Equal(g74,g76)
    c: InternalAlignment(g74,g77)
    c: InternalAlignment(g75,g77)
    c: InternalAlignment(g76,g77)
    c: InternalAlignment(g78,g77)
    c: InternalAlignment(g79,g77)
    c: Block(g77)
    c: Weight(g80) = 1
    c: Equal(g80,g81)
    c: Equal(g80,g82)
    c: InternalAlignment(g80,g83)
    c: InternalAlignment(g81,g83)
    c: InternalAlignment(g82,g83)
    c: InternalAlignment(g84,g83)
    c: InternalAlignment(g85,g83)
    c: Block(g83)
    c: Weight(g86) = 1
    c: Equal(g86,g87)
    c: Equal(g86,g88)
    c: InternalAlignment(g86,g89)
    c: InternalAlignment(g87,g89)
    c: InternalAlignment(g88,g89)
    c: InternalAlignment(g90,g89)
    c: InternalAlignment(g91,g89)
    c: Weight(g92) = 1
    c: Equal(g92,g93)
    c: Equal(g92,g94)
    c: InternalAlignment(g92,g95)
    c: InternalAlignment(g93,g95)
    c: InternalAlignment(g94,g95)
    c: InternalAlignment(g96,g95)
    c: InternalAlignment(g97,g95)
    c: Block(g89)
    c: Block(g95)
    c: Coincident(g98,g89)
    c: Coincident(g98,g95)
    c: Vertical(g98)
    c: Coincident(g99,g89)
    c: Coincident(g99,g71)
    c: Coincident(g100,g71)
    c: Coincident(g100,g95)
    c: Weight(g101) = 1
    c: Equal(g101,g102)
    c: Equal(g101,g103)
    c: InternalAlignment(g101,g104)
    c: InternalAlignment(g102,g104)
    c: InternalAlignment(g103,g104)
    c: InternalAlignment(g105,g104)
    c: InternalAlignment(g106,g104)
    c: Weight(g107) = 1
    c: Equal(g107,g108)
    c: Equal(g107,g109)
    c: InternalAlignment(g107,g110)
    c: InternalAlignment(g108,g110)
    c: InternalAlignment(g109,g110)
    c: InternalAlignment(g111,g110)
    c: InternalAlignment(g112,g110)
    c: Block(g104)
    c: Block(g110)
    c: Coincident(g113,g104)
    c: Coincident(g113,g110)
    c: Vertical(g113)
    c: Coincident(g114,g104)
    c: Coincident(g114,g65)
    c: Coincident(g115,g65)
    c: Coincident(g115,g110)
    c: Weight(g116) = 1
    c: Equal(g116,g117)
    c: Equal(g116,g118)
    c: InternalAlignment(g116,g119)
    c: InternalAlignment(g117,g119)
    c: InternalAlignment(g118,g119)
    c: InternalAlignment(g120,g119)
    c: InternalAlignment(g121,g119)
    c: Weight(g122) = 1
    c: Equal(g122,g123)
    c: Equal(g122,g124)
    c: InternalAlignment(g122,g125)
    c: InternalAlignment(g123,g125)
    c: InternalAlignment(g124,g125)
    c: InternalAlignment(g126,g125)
    c: InternalAlignment(g127,g125)
    c: Block(g119)
    c: Block(g125)
    c: Coincident(g128,g119)
    c: Coincident(g128,g125)
    c: Vertical(g128)
    c: Coincident(g129,g125)
    c: Coincident(g129,g83)
    c: Coincident(g130,g83)
    c: Coincident(g130,g119)
    c: Weight(g131) = 1
    c: Equal(g131,g132)
    c: Equal(g131,g133)
    c: InternalAlignment(g131,g134)
    c: InternalAlignment(g132,g134)
    c: InternalAlignment(g133,g134)
    c: InternalAlignment(g135,g134)
    c: InternalAlignment(g136,g134)
    c: Weight(g137) = 1
    c: Equal(g137,g138)
    c: Equal(g137,g139)
    c: InternalAlignment(g137,g140)
    c: InternalAlignment(g138,g140)
    c: InternalAlignment(g139,g140)
    c: InternalAlignment(g141,g140)
    c: InternalAlignment(g142,g140)
    c: Block(g134)
    c: Block(g140)
    c: Coincident(g143,g134)
    c: Coincident(g143,g140)
    c: Vertical(g143)
    c: Coincident(g144,g140)
    c: Coincident(g144,g77)
    c: Coincident(g145,g77)
    c: Coincident(g145,g134)
    c: Weight(g146) = 1
    c: Equal(g146,g147)
    c: Equal(g146,g148)
    c: InternalAlignment(g146,g149)
    c: InternalAlignment(g147,g149)
    c: InternalAlignment(g148,g149)
    c: InternalAlignment(g150,g149)
    c: InternalAlignment(g151,g149)
    c: Weight(g152) = 1
    c: Equal(g152,g153)
    c: Equal(g152,g154)
    c: InternalAlignment(g152,g155)
    c: InternalAlignment(g153,g155)
    c: InternalAlignment(g154,g155)
    c: InternalAlignment(g156,g155)
    c: InternalAlignment(g157,g155)
    c: Weight(g158) = 1
    c: Equal(g158,g159)
    c: Equal(g158,g160)
    c: InternalAlignment(g158,g161)
    c: InternalAlignment(g159,g161)
    c: InternalAlignment(g160,g161)
    c: InternalAlignment(g162,g161)
    c: InternalAlignment(g163,g161)
    c: Weight(g164) = 1
    c: Equal(g164,g165)
    c: Equal(g164,g166)
    c: InternalAlignment(g164,g167)
    c: InternalAlignment(g165,g167)
    c: InternalAlignment(g166,g167)
    c: InternalAlignment(g168,g167)
    c: InternalAlignment(g169,g167)
    c: Block(g167)
    c: Block(g161)
    c: Block(g155)
    c: Block(g149)
    c: Coincident(g170,g40)
    c: Coincident(g170,g167)
    c: Coincident(g171,g167)
    c: Coincident(g171,g161)
    c: Horizontal(g171)
    c: Coincident(g172,g161)
    c: Coincident(g172,g40)
    c: Vertical(g172)
    c: Coincident(g173,g34)
    c: Coincident(g173,g155)
    c: Vertical(g173)
    c: Coincident(g174,g155)
    c: Coincident(g174,g149)
    c: Horizontal(g174)
    c: Coincident(g175,g149)
    c: Coincident(g175,g34)
    c: Weight(g176) = 1
    c: Equal(g176,g177)
    c: Equal(g176,g178)
    c: InternalAlignment(g176,g179)
    c: InternalAlignment(g177,g179)
    c: InternalAlignment(g178,g179)
    c: InternalAlignment(g180,g179)
    c: InternalAlignment(g181,g179)
    c: Weight(g182) = 1
    c: Equal(g182,g183)
    c: Equal(g182,g184)
    c: InternalAlignment(g182,g185)
    c: InternalAlignment(g183,g185)
    c: InternalAlignment(g184,g185)
    c: InternalAlignment(g186,g185)
    c: InternalAlignment(g187,g185)
    c: Weight(g188) = 1
    c: Equal(g188,g189)
    c: Equal(g188,g190)
    c: InternalAlignment(g188,g191)
    c: InternalAlignment(g189,g191)
    c: InternalAlignment(g190,g191)
    c: InternalAlignment(g192,g191)
    c: InternalAlignment(g193,g191)
    c: Weight(g194) = 1
    c: Equal(g194,g195)
    c: Equal(g194,g196)
    c: InternalAlignment(g194,g197)
    c: InternalAlignment(g195,g197)
    c: InternalAlignment(g196,g197)
    c: InternalAlignment(g198,g197)
    c: InternalAlignment(g199,g197)
    c: Block(g197)
    c: Block(g191)
    c: Block(g185)
    c: Block(g179)
    c: Coincident(g200,g197)
    c: Coincident(g200,g191)
    c: Horizontal(g200)
    c: Coincident(g201,g191)
    c: Coincident(g201,g22)
    c: Vertical(g201)
    c: Coincident(g202,g28)
    c: Coincident(g202,g185)
    c: Vertical(g202)
    c: Coincident(g203,g185)
    c: Coincident(g203,g179)
    c: Horizontal(g203)
    c: Coincident(g204,g179)
    c: Coincident(g204,g28)
    c: Coincident(g205,g22)
    c: Weight(g206) = 1
    c: Equal(g206,g207)
    c: Equal(g206,g208)
    c: InternalAlignment(g206,g209)
    c: InternalAlignment(g207,g209)
    c: InternalAlignment(g208,g209)
    c: InternalAlignment(g210,g209)
    c: InternalAlignment(g211,g209)
    c: Weight(g212) = 1
    c: Equal(g212,g213)
    c: Equal(g212,g214)
    c: InternalAlignment(g212,g215)
    c: InternalAlignment(g213,g215)
    c: InternalAlignment(g214,g215)
    c: InternalAlignment(g216,g215)
    c: InternalAlignment(g217,g215)
    c: Block(g215)
    c: Block(g209)
    c: Coincident(g218,g215)
    c: Coincident(g218,g46)
    c: Coincident(g219,g46)
    c: Coincident(g219,g209)
    c: Coincident(g220,g209)
    c: Coincident(g220,g215)
    c: Vertical(g220)
    c: Weight(g221) = 1
    c: Equal(g221,g222)
    c: Equal(g221,g223)
    c: InternalAlignment(g221,g224)
    c: InternalAlignment(g222,g224)
    c: InternalAlignment(g223,g224)
    c: InternalAlignment(g225,g224)
    c: InternalAlignment(g226,g224)
    c: Weight(g227) = 1
    c: Equal(g227,g228)
    c: Equal(g227,g229)
    c: InternalAlignment(g227,g230)
    c: InternalAlignment(g228,g230)
    c: InternalAlignment(g229,g230)
    c: InternalAlignment(g231,g230)
    c: InternalAlignment(g232,g230)
    c: Block(g230)
    c: Block(g224)
    c: Coincident(g233,g224)
    c: Coincident(g233,g52)
    c: Coincident(g234,g52)
    c: Coincident(g234,g230)
    c: Coincident(g235,g230)
    c: Coincident(g235,g224)
    c: Vertical(g235)
    c: Horizontal(g236)
    c: Block(g236)
    c: Vertical(g237)
    c: Block(g237)
    c: Block(g238)
    c: Weight(g239) = 1
    c: Equal(g239,g240)
    c: Equal(g239,g241)
    c: InternalAlignment(g239,g242)
    c: InternalAlignment(g240,g242)
    c: InternalAlignment(g241,g242)
    c: InternalAlignment(g243,g242)
    c: InternalAlignment(g244,g242)
    c: Weight(g245) = 1
    c: Equal(g245,g246)
    c: Equal(g245,g247)
    c: InternalAlignment(g245,g248)
    c: InternalAlignment(g246,g248)
    c: InternalAlignment(g247,g248)
    c: InternalAlignment(g249,g248)
    c: InternalAlignment(g250,g248)
    c: Weight(g251) = 1
    c: Equal(g251,g252)
    c: Equal(g251,g253)
    c: InternalAlignment(g251,g254)
    c: InternalAlignment(g252,g254)
    c: InternalAlignment(g253,g254)
    c: InternalAlignment(g255,g254)
    c: InternalAlignment(g256,g254)
    c: Weight(g257) = 1
    c: Equal(g257,g258)
    c: Equal(g257,g259)
    c: InternalAlignment(g257,g260)
    c: InternalAlignment(g258,g260)
    c: InternalAlignment(g259,g260)
    c: InternalAlignment(g261,g260)
    c: InternalAlignment(g262,g260)
    c: Block(g242)
    c: Block(g248)
    c: Block(g254)
    c: Block(g260)
    c: Coincident(g263,g248)
    c: Coincident(g263,g242)
    c: Horizontal(g263)
    c: Block(g205)
    c: Weight(g264) = 1
    c: Equal(g264,g265)
    c: Equal(g264,g266)
    c: InternalAlignment(g264,g267)
    c: InternalAlignment(g265,g267)
    c: InternalAlignment(g266,g267)
    c: InternalAlignment(g268,g267)
    c: InternalAlignment(g269,g267)
    c: Weight(g270) = 1
    c: Equal(g270,g271)
    c: Equal(g270,g272)
    c: InternalAlignment(g270,g273)
    c: InternalAlignment(g271,g273)
    c: InternalAlignment(g272,g273)
    c: InternalAlignment(g274,g273)
    c: InternalAlignment(g275,g273)
    c: Weight(g276) = 1
    c: Equal(g276,g277)
    c: Equal(g276,g278)
    c: InternalAlignment(g276,g279)
    c: InternalAlignment(g277,g279)
    c: InternalAlignment(g278,g279)
    c: InternalAlignment(g280,g279)
    c: InternalAlignment(g281,g279)
    c: Weight(g282) = 1
    c: Equal(g282,g283)
    c: Equal(g282,g284)
    c: InternalAlignment(g282,g285)
    c: InternalAlignment(g283,g285)
    c: InternalAlignment(g284,g285)
    c: InternalAlignment(g286,g285)
    c: InternalAlignment(g287,g285)
    c: Block(g267)
    c: Block(g273)
    c: Block(g279)
    c: Block(g285)
    c: Coincident(g288,g279)
    c: Coincident(g288,g285)
    c: Horizontal(g288)
    c: Coincident(g289,g285)
    c: Coincident(g289,g267)
    c: Vertical(g289)
    c: Coincident(g290,g267)
    c: Coincident(g290,g273)
    c: Coincident(g291,g273)
    c: Coincident(g291,g279)
    c: Vertical(g291)
FEATURE [Sketcher::SketchObject] Sketch001
  FullyConstrained = true
  MapMode = 4
  Placement = pos=(0,0,0) rot=(0.57735,0.57735,0.57735;2.0944rad)
  Support = -> [Sketch]
  sketch-geometry (46):
    g0: BSplineCurve PolesCount=3 KnotsCount=2 Degree=2 IsPeriodic=0
    g1: ArcOfCircle CenterX=73.1223 CenterY=-32.291 CenterZ=0 NormalX=0 NormalY=0 NormalZ=1 AngleXU=0 Radius=13 StartAngle=5.92268 EndAngle=9.06428
    g2: ArcOfCircle CenterX=66.7816 CenterY=-49.1439 CenterZ=0 NormalX=0 NormalY=0 NormalZ=1 AngleXU=0 Radius=13 StartAngle=2.78068 EndAngle=5.92131
    g3: ArcOfCircle CenterX=55.9263 CenterY=-78.1807 CenterZ=0 NormalX=0 NormalY=0 NormalZ=1 AngleXU=0 Radius=13 StartAngle=5.92268 EndAngle=9.06428
    g4: ArcOfCircle CenterX=49.5884 CenterY=-95.0342 CenterZ=0 NormalX=0 NormalY=0 NormalZ=1 AngleXU=0 Radius=13 StartAngle=2.78068 EndAngle=5.92131
    g5: ArcOfCircle CenterX=38.7206 CenterY=-124.067 CenterZ=0 NormalX=0 NormalY=0 NormalZ=1 AngleXU=0 Radius=13 StartAngle=5.92268 EndAngle=9.06428
    g6: ArcOfCircle CenterX=32.3875 CenterY=-140.92 CenterZ=0 NormalX=0 NormalY=0 NormalZ=1 AngleXU=0 Radius=13 StartAngle=2.78068 EndAngle=5.92131
    g7: ArcOfCircle CenterX=21.4715 CenterY=-169.934 CenterZ=0 NormalX=0 NormalY=0 NormalZ=1 AngleXU=0 Radius=13 StartAngle=5.92268 EndAngle=9.06428
    g8: ArcOfCircle CenterX=15.1336 CenterY=-186.787 CenterZ=0 NormalX=0 NormalY=0 NormalZ=1 AngleXU=0 Radius=13 StartAngle=2.78068 EndAngle=5.92131
    g9-g12: Circle x4 (B-spline internal-alignment scaffolding for g13; pole/knot coordinates omitted)
    g13: BSplineCurve PolesCount=4 KnotsCount=2 Degree=3 IsPeriodic=0
    g14: GeomPoint X=28.8094 Y=-19.0875 Z=0
    g15: GeomPoint X=47.0443 Y=-50.4712 Z=0
    g16: Circle CenterX=53.5586 CenterY=-23.2695 CenterZ=0 NormalX=0 NormalY=0 NormalZ=1 AngleXU=0 Radius=3.24518
    g17: Circle CenterX=-195.441 CenterY=-127.082 CenterZ=0 NormalX=0 NormalY=0 NormalZ=1 AngleXU=0 Radius=1
    g18: Circle CenterX=-8.24091 CenterY=-197.481 CenterZ=0 NormalX=0 NormalY=0 NormalZ=1 AngleXU=0 Radius=1
    g19: Circle CenterX=12.8789 CenterY=-141.321 CenterZ=0 NormalX=0 NormalY=0 NormalZ=1 AngleXU=0 Radius=1
    g20: BSplineCurve PolesCount=3 KnotsCount=2 Degree=2 IsPeriodic=0
    g21: GeomPoint X=-195.441 Y=-127.082 Z=0
    g22: GeomPoint X=12.8789 Y=-141.321 Z=0
    g23: Circle CenterX=-12.8016 CenterY=-179.036 CenterZ=0 NormalX=0 NormalY=0 NormalZ=1 AngleXU=0 Radius=10.5072
    g24: Circle CenterX=0.933922 CenterY=-166.43 CenterZ=0 NormalX=0 NormalY=0 NormalZ=1 AngleXU=0 Radius=3.26661
    g25: Circle CenterX=-33.5518 CenterY=-176.44 CenterZ=0 NormalX=0 NormalY=0 NormalZ=1 AngleXU=0 Radius=5.64388
    g26: Circle CenterX=-47.2366 CenterY=-173.859 CenterZ=0 NormalX=0 NormalY=0 NormalZ=1 AngleXU=0 Radius=3.01653
    g27: Circle CenterX=-56.2595 CenterY=-171.456 CenterZ=0 NormalX=0 NormalY=0 NormalZ=1 AngleXU=0 Radius=2.12826
    g28: ArcOfCircle CenterX=51.2151 CenterY=-198.473 CenterZ=0 NormalX=0 NormalY=0 NormalZ=1 AngleXU=0 Radius=20 StartAngle=2.78189 EndAngle=4.35269
    g29: LineSegment StartX=32.4951 StartY=-191.433 StartZ=0 EndX=94.6578 EndY=-26.1352 EndZ=0
    g30: LineSegment StartX=43.1192 StartY=-220.001 StartZ=0 EndX=-196.497 EndY=-129.89 EndZ=0
    g31: LineSegment StartX=43.1192 StartY=-220.001 StartZ=0 EndX=44.1752 EndY=-217.193 EndZ=0
    g32: LineSegment StartX=117.223 StartY=-19.0875 StartZ=0 EndX=117.223 EndY=-16.0875 EndZ=0
    g33: LineSegment StartX=117.223 StartY=-16.0875 StartZ=0 EndX=17.2232 EndY=-16.0875 EndZ=0
    g34: LineSegment StartX=17.2232 StartY=-16.0875 StartZ=0 EndX=17.2232 EndY=-19.0875 EndZ=0
    g35: LineSegment StartX=28.8094 StartY=-19.0875 StartZ=0 EndX=17.2232 EndY=-19.0875 EndZ=0
    g36: LineSegment StartX=47.0443 StartY=-50.4712 StartZ=0 EndX=12.8789 EndY=-141.321 EndZ=0
    g37: LineSegment StartX=-195.441 StartY=-127.082 StartZ=0 EndX=-196.497 EndY=-129.89 EndZ=0
    g38: LineSegment StartX=85.2866 StartY=-36.8766 StartZ=0 EndX=78.9396 EndY=-53.7463 EndZ=0
    g39: LineSegment StartX=60.9579 StartY=-27.7053 StartZ=0 EndX=54.6191 EndY=-44.5532 EndZ=0
    g40: LineSegment StartX=68.0907 StartY=-82.7664 StartZ=0 EndX=61.7465 EndY=-99.6365 EndZ=0
    g41: LineSegment StartX=43.7619 StartY=-73.595 StartZ=0 EndX=37.426 EndY=-90.4435 EndZ=0
    g42: LineSegment StartX=50.885 StartY=-128.652 StartZ=0 EndX=44.5456 EndY=-145.522 EndZ=0
    g43: LineSegment StartX=26.5562 StartY=-119.481 StartZ=0 EndX=20.2251 EndY=-136.329 EndZ=0
    g44: LineSegment StartX=9.3071 StartY=-165.349 StartZ=0 EndX=2.97115 EndY=-182.197 EndZ=0
    g45: LineSegment StartX=33.6358 StartY=-174.52 StartZ=0 EndX=27.2917 EndY=-191.39 EndZ=0
  constraints (71):
    c: Block(g0)
    c: Block(g1)
    c: Block(g2)
    c: Block(g4)
    c: Block(g3)
    c: Block(g6)
    c: Block(g5)
    c: Block(g8)
    c: Block(g7)
    c: Weight(g9) = 1
    c: Equal(g9,g10)
    c: Equal(g9,g11)
    c: Equal(g9,g12)
    c: InternalAlignment(g9-g12 -> g13) x4
    c: InternalAlignment(g14,g13)
    c: InternalAlignment(g15,g13)
    c: Block(g16)
    c: Weight(g17) = 1
    c: Equal(g17,g18)
    c: Equal(g17,g19)
    c: InternalAlignment(g17,g20)
    c: InternalAlignment(g18,g20)
    c: InternalAlignment(g19,g20)
    c: InternalAlignment(g21,g20)
    c: InternalAlignment(g22,g20)
    c: Block(g20)
    c: Block(g23)
    c: Block(g24)
    c: Block(g25)
    c: Block(g26)
    c: Block(g27)
    c: Block(g28)
    c: Coincident(g29,g28)
    c: Coincident(g29,g0)
    c: Block(g13)
    c: Coincident(g31,g30)
    c: Coincident(g31,g28)
    c: Block(g31)
    c: Coincident(g32,g0)
    c: Vertical(g32)
    c: Coincident(g33,g32)
    c: Horizontal(g33)
    c: Coincident(g34,g33)
    c: Vertical(g34)
    c: Block(g33)
    c: Coincident(g35,g13)
    c: Coincident(g35,g34)
    c: Horizontal(g35)
    c: Coincident(g36,g13)
    c: Coincident(g36,g20)
    c: Coincident(g37,g20)
    c: Coincident(g37,g30)
    c: Block(g30)
    c: Coincident(g38,g1)
    c: Coincident(g38,g2)
    c: Coincident(g39,g1)
    c: Coincident(g39,g2)
    c: Coincident(g40,g3)
    c: Coincident(g40,g4)
    c: Coincident(g41,g3)
    c: Coincident(g41,g4)
    c: Coincident(g42,g5)
    c: Coincident(g42,g6)
    c: Coincident(g43,g5)
    c: Coincident(g43,g6)
    c: Coincident(g44,g7)
    c: Coincident(g44,g8)
    c: Coincident(g45,g7)
    c: Coincident(g45,g8)
    c: Distance(g30) = 256
    c: Distance(g33) = 100
FEATURE [Part::Extrusion] Extrude002
  Base = -> Sketch001
  Dir = (1,0,0)
  DirMode = 2
  FaceMakerClass = Part::FaceMakerBullseye
  LengthFwd = 8
  LengthRev = 0
  Solid = true
  Symmetric = false
FEATURE [Sketcher::SketchObject] Sketch002
  FullyConstrained = true
  sketch-geometry (20):
    g0: LineSegment StartX=-2.77179 StartY=-200.304 StartZ=0 EndX=5.22821 EndY=-200.304 EndZ=0
    g1: LineSegment StartX=5.22821 StartY=-200.304 StartZ=0 EndX=5.22821 EndY=-197.304 EndZ=0
    g2: LineSegment StartX=-2.77179 StartY=-200.304 StartZ=0 EndX=-2.77179 EndY=-197.304 EndZ=0
    g3: LineSegment StartX=5.22821 StartY=-197.304 StartZ=0 EndX=8.22821 EndY=-197.304 EndZ=0
    g4: LineSegment StartX=-2.77179 StartY=-197.304 StartZ=0 EndX=-5.77179 EndY=-197.304 EndZ=0
    g5: LineSegment StartX=19.2282 StartY=-203.304 StartZ=0 EndX=19.2282 EndY=-206.304 EndZ=0
    g6: LineSegment StartX=-16.7718 StartY=-203.304 StartZ=0 EndX=-16.7718 EndY=-206.304 EndZ=0
    g7: LineSegment StartX=-16.7718 StartY=-206.304 StartZ=0 EndX=19.2282 EndY=-206.304 EndZ=0
    g8: Circle CenterX=-16.7718 CenterY=-203.304 CenterZ=0 NormalX=0 NormalY=0 NormalZ=1 AngleXU=0 Radius=1
    g9: Circle CenterX=-5.77179 CenterY=-203.304 CenterZ=0 NormalX=0 NormalY=0 NormalZ=1 AngleXU=0 Radius=1
    g10: Circle CenterX=-5.77179 CenterY=-197.304 CenterZ=0 NormalX=0 NormalY=0 NormalZ=1 AngleXU=0 Radius=1
    g11: BSplineCurve PolesCount=3 KnotsCount=2 Degree=2 IsPeriodic=0
    g12: GeomPoint X=-16.7718 Y=-203.304 Z=0
    g13: GeomPoint X=-5.77179 Y=-197.304 Z=0
    g14: Circle CenterX=19.2282 CenterY=-203.304 CenterZ=0 NormalX=0 NormalY=0 NormalZ=1 AngleXU=0 Radius=1
    g15: Circle CenterX=8.22821 CenterY=-203.304 CenterZ=0 NormalX=0 NormalY=0 NormalZ=1 AngleXU=0 Radius=1
    g16: Circle CenterX=8.22821 CenterY=-197.304 CenterZ=0 NormalX=0 NormalY=0 NormalZ=1 AngleXU=0 Radius=1
    g17: BSplineCurve PolesCount=3 KnotsCount=2 Degree=2 IsPeriodic=0
    g18: GeomPoint X=19.2282 Y=-203.304 Z=0
    g19: GeomPoint X=8.22821 Y=-197.304 Z=0
  constraints (41):
    c: Horizontal(g0)
    c: Distance(g0) = 8
    c: Coincident(g1,g0)
    c: Vertical(g1)
    c: Distance(g1) = 3
    c: Coincident(g2,g0)
    c: Vertical(g2)
    c: Distance(g2) = 3
    c: Coincident(g3,g1)
    c: Horizontal(g3)
    c: Distance(g3) = 3
    c: Coincident(g4,g2)
    c: Horizontal(g4)
    c: Distance(g4) = 3
    c: Vertical(g5)
    c: Vertical(g6)
    c: Coincident(g7,g6)
    c: Coincident(g7,g5)
    c: Weight(g8) = 1
    c: Equal(g8,g9)
    c: Equal(g8,g10)
    c: Coincident(g11,g4)
    c: InternalAlignment(g8,g11)
    c: InternalAlignment(g9,g11)
    c: InternalAlignment(g10,g11)
    c: InternalAlignment(g12,g11)
    c: InternalAlignment(g13,g11)
    c: Coincident(g17,g5)
    c: Weight(g14) = 1
    c: Equal(g14,g15)
    c: Equal(g14,g16)
    c: Coincident(g17,g3)
    c: InternalAlignment(g14,g17)
    c: InternalAlignment(g15,g17)
    c: InternalAlignment(g16,g17)
    c: InternalAlignment(g18,g17)
    c: InternalAlignment(g19,g17)
    c: Block(g7)
    c: Block(g17)
    c: Block(g11)
    c: Block(g6)
FEATURE [Part::Extrusion] Extrude003
  Base = -> Sketch002
  Dir = (0,0,1)
  DirMode = 2
  FaceMakerClass = Part::FaceMakerBullseye
  LengthFwd = 260
  LengthRev = 0
  Solid = true
  Symmetric = false
FEATURE [Part::Extrusion] Extrude
  Base = -> Sketch
  Dir = (0,0,1)
  DirMode = 2
  FaceMakerClass = Part::FaceMakerBullseye
  LengthFwd = 14
  LengthRev = 0
  Solid = true
  Symmetric = false
